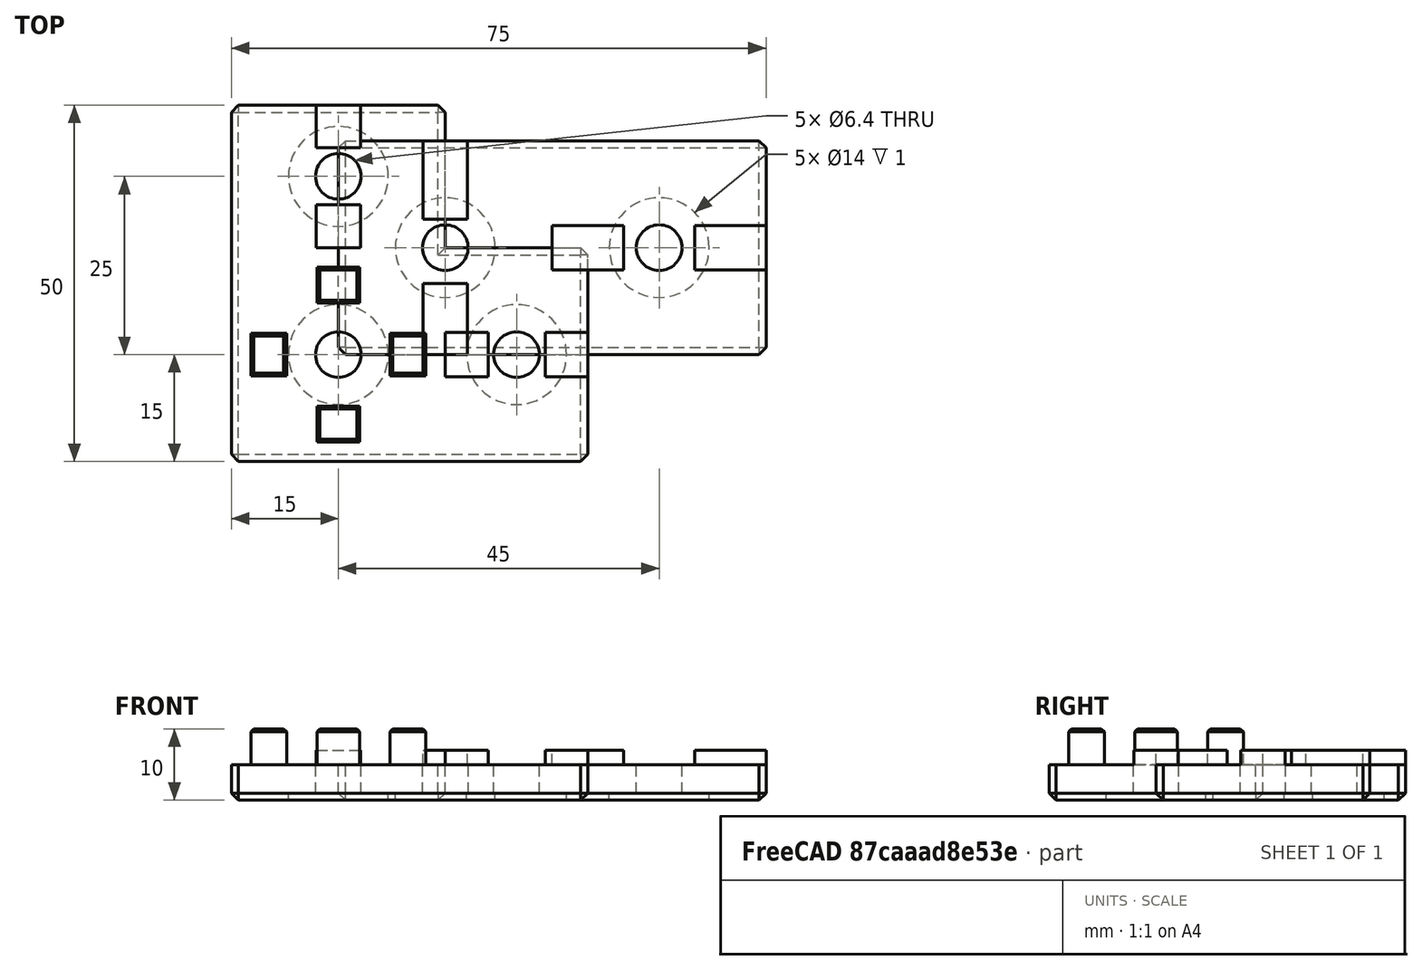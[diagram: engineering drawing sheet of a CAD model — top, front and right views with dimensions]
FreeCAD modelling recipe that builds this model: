
FCSTD DOCUMENT  (FreeCAD 0.18R16146 (Git))
Label: joiner
License: All rights reserved
LicenseURL: http://en.wikipedia.org/wiki/All_rights_reserved
objects: Part::Box×10, Part::Cylinder×10, Part::MultiFuse×6, Part::Feature×2, Part::Chamfer×2, Part::Cut×2, Part::MultiCommon×1
note: 33 computed .brp shape members not serialized (recipe doc carries the construction recipe); baked Part::Feature solids carry a one-line shape summary decoded from their .brp

FEATURE [Part::Box] Box  label="Cube"
  AttacherType = Attacher::AttachEngine3D
  Height = 5
  Length = 60
  Width = 30
FEATURE [Part::Cylinder] Cylinder
  Angle = 360
  AttacherType = Attacher::AttachEngine3D
  Height = 10
  Placement = pos=(15,15,0) rot=(0,0,1;0rad)
  Radius = 3.2
FEATURE [Part::Cylinder] Cylinder001
  Angle = 360
  AttacherType = Attacher::AttachEngine3D
  Height = 10
  Placement = pos=(45,15,0) rot=(0,0,1;0rad)
  Radius = 3.2
FEATURE [Part::Box] Box001  label="Cube001"
  AttacherType = Attacher::AttachEngine3D
  Height = 3
  Length = 6.2
  Placement = pos=(11.9,0,4) rot=(0,0,1;0rad)
  Width = 10
FEATURE [Part::Box] Box002  label="Cube002"
  AttacherType = Attacher::AttachEngine3D
  Height = 3
  Length = 6.2
  Placement = pos=(11.9,19,4) rot=(0,0,1;0rad)
  Width = 11
FEATURE [Part::Box] Box003  label="Cube003"
  AttacherType = Attacher::AttachEngine3D
  Height = 3
  Length = 10
  Placement = pos=(50,11.9,4) rot=(0,0,1;0rad)
  Width = 6.2
FEATURE [Part::Box] Box004  label="Cube004"
  AttacherType = Attacher::AttachEngine3D
  Height = 3
  Length = 10
  Placement = pos=(30,11.9,4) rot=(0,0,1;0rad)
  Width = 6.2
FEATURE [Part::Cylinder] Cylinder002
  Angle = 360
  AttacherType = Attacher::AttachEngine3D
  Height = 1
  Placement = pos=(15,15,0) rot=(0,0,1;0rad)
  Radius = 7
FEATURE [Part::Cylinder] Cylinder003
  Angle = 360
  AttacherType = Attacher::AttachEngine3D
  Height = 1
  Placement = pos=(45,15,0) rot=(0,0,1;0rad)
  Radius = 7
FEATURE [Part::MultiFuse] Fusion001
  Shapes = -> [Box002,Box001,Box004,Box003]
FEATURE [Part::Feature] Cut004001  label="Cut005"
  shape: bbox 50 x 50 x 15 mm, 78 faces (baked)
FEATURE [Part::Box] Box005  label="Cube005"
  AttacherType = Attacher::AttachEngine3D
  Height = 10
  Length = 30
  Placement = pos=(-15,-15,0) rot=(0,0,1;0rad)
  Width = 30
FEATURE [Part::MultiCommon] Common
  Placement = pos=(0,0,5) rot=(0,0,1;0rad)
  Shapes = -> [Box005,Cut004001]
FEATURE [Part::Cylinder] Cylinder004
  Angle = 360
  AttacherType = Attacher::AttachEngine3D
  Height = 10
  Placement = pos=(0,25,0) rot=(0,0,1;0rad)
  Radius = 3.2
FEATURE [Part::Cylinder] Cylinder005
  Angle = 360
  AttacherType = Attacher::AttachEngine3D
  Height = 10
  Placement = pos=(25,0,0) rot=(0,0,1;0rad)
  Radius = 3.2
FEATURE [Part::Cylinder] Cylinder006
  Angle = 360
  AttacherType = Attacher::AttachEngine3D
  Height = 1
  Placement = pos=(25,0,0) rot=(0,0,1;0rad)
  Radius = 7
FEATURE [Part::Cylinder] Cylinder007
  Angle = 360
  AttacherType = Attacher::AttachEngine3D
  Height = 1
  Placement = pos=(0,25,0) rot=(0,0,1;0rad)
  Radius = 7
FEATURE [Part::Cylinder] Cylinder008
  Angle = 360
  AttacherType = Attacher::AttachEngine3D
  Height = 10
  Radius = 3.2
FEATURE [Part::Cylinder] Cylinder009
  Angle = 360
  AttacherType = Attacher::AttachEngine3D
  Height = 1
  Radius = 7
FEATURE [Part::Box] Box009  label="Cube009"
  AttacherType = Attacher::AttachEngine3D
  Height = 3
  Length = 6
  Placement = pos=(15,-3.1,4) rot=(0,0,1;0rad)
  Width = 6.2
FEATURE [Part::Box] Box010  label="Cube010"
  AttacherType = Attacher::AttachEngine3D
  Height = 3
  Length = 6
  Placement = pos=(29,-3.1,4) rot=(0,0,1;0rad)
  Width = 6.2
FEATURE [Part::Box] Box011  label="Cube011"
  AttacherType = Attacher::AttachEngine3D
  Height = 3
  Length = 6.2
  Placement = pos=(-3.1,15,4) rot=(0,0,1;0rad)
  Width = 6
FEATURE [Part::Box] Box012  label="Cube012"
  AttacherType = Attacher::AttachEngine3D
  Height = 3
  Length = 6.2
  Placement = pos=(-3.1,29,4) rot=(0,0,1;0rad)
  Width = 6
FEATURE [Part::MultiFuse] Fusion
  Shapes = -> [Cylinder,Cylinder001,Cylinder002,Cylinder003]
FEATURE [Part::Chamfer] Chamfer
  Base = -> Box
  Edges = 8 edges r=1: [Edge1,Edge3,Edge4,Edge5,Edge7,Edge8,Edge9,Edge11]
FEATURE [Part::Cut] Cut
  Base = -> Chamfer
  Tool = -> Fusion
FEATURE [Part::MultiFuse] Fusion006  label="I-shape"
  Shapes = -> [Cut,Fusion001]
FEATURE [Part::MultiFuse] Fusion007
  Shapes = -> [Cylinder007,Cylinder006,Cylinder005,Cylinder004,Cylinder008,Cylinder009]
FEATURE [Part::Feature] Fusion004001  label="Fusion008"
  shape: bbox 50 x 50 x 10 mm, 44 faces (baked)
FEATURE [Part::Chamfer] Chamfer001
  Base = -> Fusion004001
  Edges = 11 edges r=1: [Edge1,Edge2,Edge4,Edge7,Edge8,Edge9,Edge11,Edge13,Edge14,Edge15,Edge98]
FEATURE [Part::Cut] Cut004002
  Base = -> Chamfer001
  Tool = -> Fusion007
FEATURE [Part::MultiFuse] Fusion004002
  Shapes = -> [Box012,Box011,Box010,Box009]
FEATURE [Part::MultiFuse] Fusion004003  label="L-shape"
  Shapes = -> [Fusion004002,Cut004002,Common]
